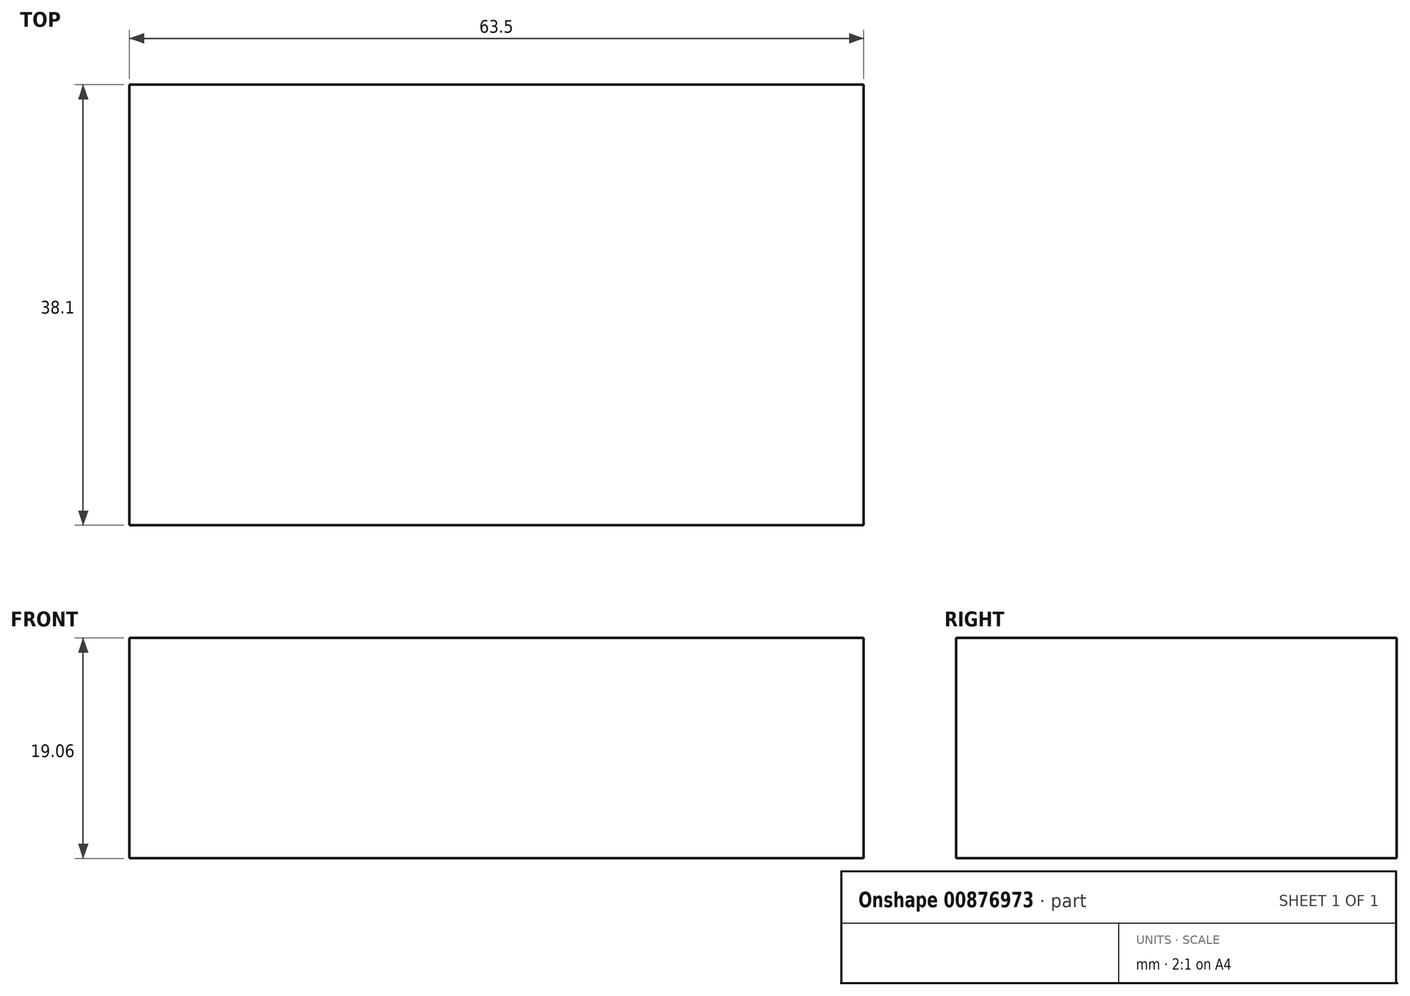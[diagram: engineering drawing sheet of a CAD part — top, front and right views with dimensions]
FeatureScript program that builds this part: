
annotation { "Feature Type Name" : "Feature", "Feature Type Description" : "" }
export const myFeature = defineFeature(function(context is Context, id is Id, definition is map)
    precondition{}
    {
        {
            var Q0;
            Q0=qCreatedBy(makeId("Right.planeOp"),FACE);
            var sketch = newSketch(context, id + "F0", { "sketchPlane" : qUnion([Q0])});
            skLineSegment(sketch, "E0.bottom", {"start": v(19.05, 9.53) * mm, "end": v(-19.05, 9.53) * mm});
            skLineSegment(sketch, "E0.top", {"start": v(19.05, -9.53) * mm, "end": v(-19.05, -9.53) * mm});
            skLineSegment(sketch, "E0.left", {"start": v(19.05, 9.53) * mm, "end": v(19.05, -9.53) * mm});
            skLineSegment(sketch, "E0.right", {"start": v(-19.05, 9.53) * mm, "end": v(-19.05, -9.53) * mm});
            skPoint(sketch, "E0.middle", {"position": v(0, 0) * mm});
            skSolve(sketch);
        }
        {
            var Q0;
            Q0=makeQuery(id+"F0.imprint","IMPRINT",FACE,{"disambiguationData":[TD([[makeQuery(id+"F0.imprint","IMPRINT",EDGE,{"derivedFrom":sQuery(id+"F0.wireOp",EDGE,"E0.bottom")}),1.0]])]});
            extrude(context, id + "F1", {"entities" : qUnion([Q0]), "depth" : 63.5 * mm, "offsetDistance" : 25.4 * mm});
        }
    });
